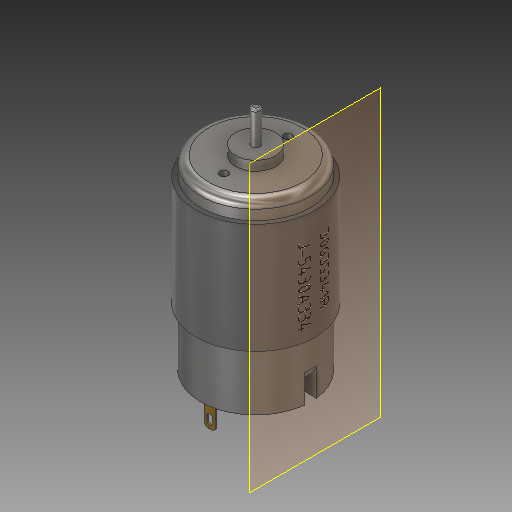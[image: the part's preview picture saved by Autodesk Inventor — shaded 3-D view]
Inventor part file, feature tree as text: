
AUTODESK INVENTOR PART (.ipt)
format: ipt  version: 2018.2 (Build 222227000, 227)  size: 287,744 bytes
history: native  units: mm
features: sketch x7, fillet x4, extrude x4, revolve x2, other x2, hole x1, plane x1
ambient origin geometry x8: Origin, YZ Plane, XZ Plane, XY Plane, X Axis, Y Axis, Z Axis, Center Point
bodies: Solid1 (feature_tree), Solid2 (feature_tree)
feature tree (21):
  sketch  "Sketch1"  dims[d0=2.23mm d1=5.6mm]
  revolve  "Revolution1"  [1 undecoded]
  revolve  "Revolution2"  [1 undecoded]
  fillet  "Fillet1"  Radius=2.1mm
  fillet  "Fillet2"  Radius=10.0mm
  hole  "Hole1"  [1 undecoded]
  extrude  "Extrusion1"  Depth=14.5mm
  fillet  "Fillet3"  Radius=27.5mm
  extrude  "Extrusion2"  TaperAngle=90.0deg  [1 undecoded]
  extrude  "Extrusion3"  Depth=2.0mm
  fillet  "Fillet4"  Radius=0.5mm
  plane  "Work Plane1"
  other  "Decal1"
  extrude  "Extrusion4"  Depth=5.0mm
  sketch  "Sketch2"  dims[d2=8.2mm d3=2.36mm d4=2.1mm d5=10.0mm]
  sketch  "Sketch3"  dims[d6=10.0mm d7=46.5mm]
  sketch  "Sketch4"  dims[d8=27.54mm d9=14.5mm d10=27.5mm]
  sketch  "Sketch5"  dims[d11=29.73mm d12=90.0deg]
  sketch  "Sketch6"  dims[d13=345.0deg d14=2.0mm d15=0.5mm]
  other  "Image1"
  sketch  "Sketch7"  dims[d16=10.5mm d17=8.0mm d18=8.0mm d19=2.0mm d20=6.0mm d21=4.0mm d22=2.0mm d23=90.0deg d24=8.0mm d25=20.594885mm d26=0.4mm d27=2.8mm d28=11.5mm d29=11.5mm d30=0.4mm d31=7.0mm d32=0.0mm d33=1.0mm d34=1.0mm d35=1.5mm d36=2.0mm d37=7.0mm d38=0.0mm d39=2.96mm d40=2.96mm d41=5.0mm d42=0.0mm d43=2.0mm d66=1.83mm d68=16.93mm d69=5.0mm d70=0.0mm]
note: 4 required parameter values undecoded (feature->parameter linkage not recoverable at this tier; creation-order binding heuristic only, values carry confidence <= 0.55)